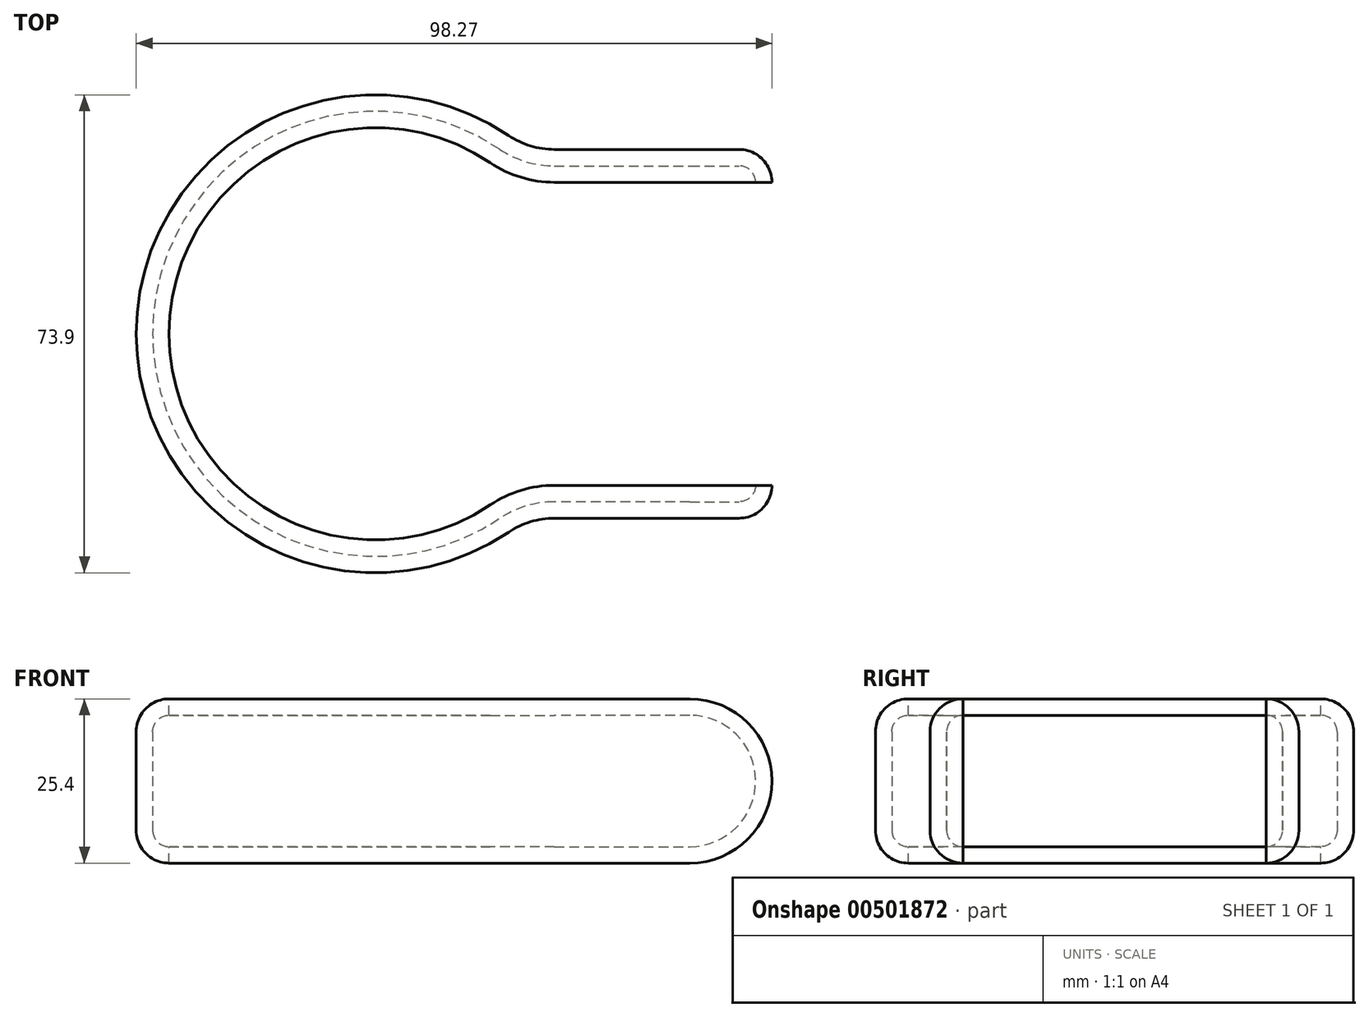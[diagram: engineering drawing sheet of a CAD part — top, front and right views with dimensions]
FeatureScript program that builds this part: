
annotation { "Feature Type Name" : "Feature", "Feature Type Description" : "" }
export const myFeature = defineFeature(function(context is Context, id is Id, definition is map)
    precondition{}
    {
        {
            var Q0;
            Q0=qCreatedBy(makeId("Top.planeOp"),FACE);
            var sketch = newSketch(context, id + "F0", { "sketchPlane" : qUnion([Q0])});
            skArc(sketch, "E0", {"start": v(23.51, 28.51) * mm, "mid": v(-36.95, 0) * mm, "end": v(23.51, -28.51) * mm});
            skLineSegment(sketch, "E1", {"start": v(23.51, -28.51) * mm, "end": v(61.32, -28.51) * mm});
            skLineSegment(sketch, "E2", {"start": v(23.51, 28.51) * mm, "end": v(61.32, 28.51) * mm});
            skLineSegment(sketch, "E3", {"start": v(61.32, 28.51) * mm, "end": v(61.32, -28.51) * mm});
            skSolve(sketch);
        }
        {
            var Q0;
            Q0 = qSketchRegion(id + "F0", true);
            extrude(context, id + "F1", {"entities" : qUnion([Q0]), "endBound" : BoundingType.SYMMETRIC, "depth" : 25.4 * mm});
        }
        {
            var Q0;
            Q0=makeQuery(id+"F1.opExtrude","CAP_EDGE",EDGE,{"disambiguationData":[OSD([sQuery(id+"F0.wireOp",EDGE,"E3")])],"isStart":false});
            var Q1;
            Q1=makeQuery(id+"F1.opExtrude","CAP_EDGE",EDGE,{"disambiguationData":[OSD([sQuery(id+"F0.wireOp",EDGE,"E3")])],"isStart":true});
            var Q2;
            Q2=makeQuery(id+"F1.opExtrude","SWEPT_EDGE",EDGE,{"disambiguationData":[OSD([sQuery(id+"F0.wireOp",EDGE,"E0"),sQuery(id+"F0.wireOp",EDGE,"E1")])]});
            var Q3;
            Q3=makeQuery(id+"F1.opExtrude","SWEPT_EDGE",EDGE,{"disambiguationData":[OSD([sQuery(id+"F0.wireOp",EDGE,"E0"),sQuery(id+"F0.wireOp",EDGE,"E2")])]});
            fillet(context, id + "F2", {"entities" : qUnion([Q0, Q1, Q2, Q3]), "radius" : 12.7 * mm, "tangentPropagation" : true, "allowEdgeOverflow" : false});
        }
        {
            var Q0;
            Q0=makeQuery(id+"F1.opExtrude","CAP_EDGE",EDGE,{"disambiguationData":[OSD([sQuery(id+"F0.wireOp",EDGE,"E0")])],"isStart":false});
            fillet(context, id + "F3", {"entities" : qUnion([Q0]), "radius" : 5.08 * mm, "tangentPropagation" : true, "allowEdgeOverflow" : false});
        }
        {
            var Q0;
            Q0=makeQuery(id+"F1.opExtrude","CAP_FACE",FACE,{"disambiguationData":[OSD([sQuery(id+"F0.wireOp",EDGE,"E0"),sQuery(id+"F0.wireOp",EDGE,"E1"),sQuery(id+"F0.wireOp",EDGE,"E2"),sQuery(id+"F0.wireOp",EDGE,"E3")])],"isStart":false});
            var Q1;
            Q1=makeQuery(id+"F2.opFillet","BLEND_FACE",FACE,{"disambiguationData":[OSD([sQuery(id+"F0.wireOp",EDGE,"E3")])]});
            var Q2;
            Q2=makeQuery(id+"F1.opExtrude","CAP_FACE",FACE,{"disambiguationData":[OSD([sQuery(id+"F0.wireOp",EDGE,"E0"),sQuery(id+"F0.wireOp",EDGE,"E1"),sQuery(id+"F0.wireOp",EDGE,"E2"),sQuery(id+"F0.wireOp",EDGE,"E3")])],"isStart":true});
            shell(context, id + "F4", {"entities" : qUnion([Q0, Q1, Q2]), "thickness" : 2.54 * mm});
        }
    });
